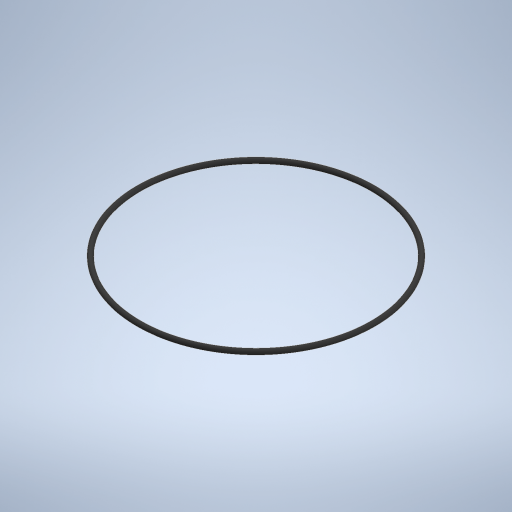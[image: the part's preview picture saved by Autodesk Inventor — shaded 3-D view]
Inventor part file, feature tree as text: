
AUTODESK INVENTOR PART (.ipt)
format: ipt  version: 2024.3 (Build 283343000, 343)  size: 258,560 bytes
history: native  units: mm
features: other x1, revolve x1, sketch x1
ambient origin geometry x8: Origin, YZ Plane, XZ Plane, XY Plane, X Axis, Y Axis, Z Axis, Center Point
bodies: Body1 (feature_tree)
feature tree (3):
  other  "Sólido1"
  revolve  "Revolución1"  Angle=360.0deg
  sketch  "Boceto1"  dims[d0=1.78mm d2=360.0deg d3=41.135mm]
